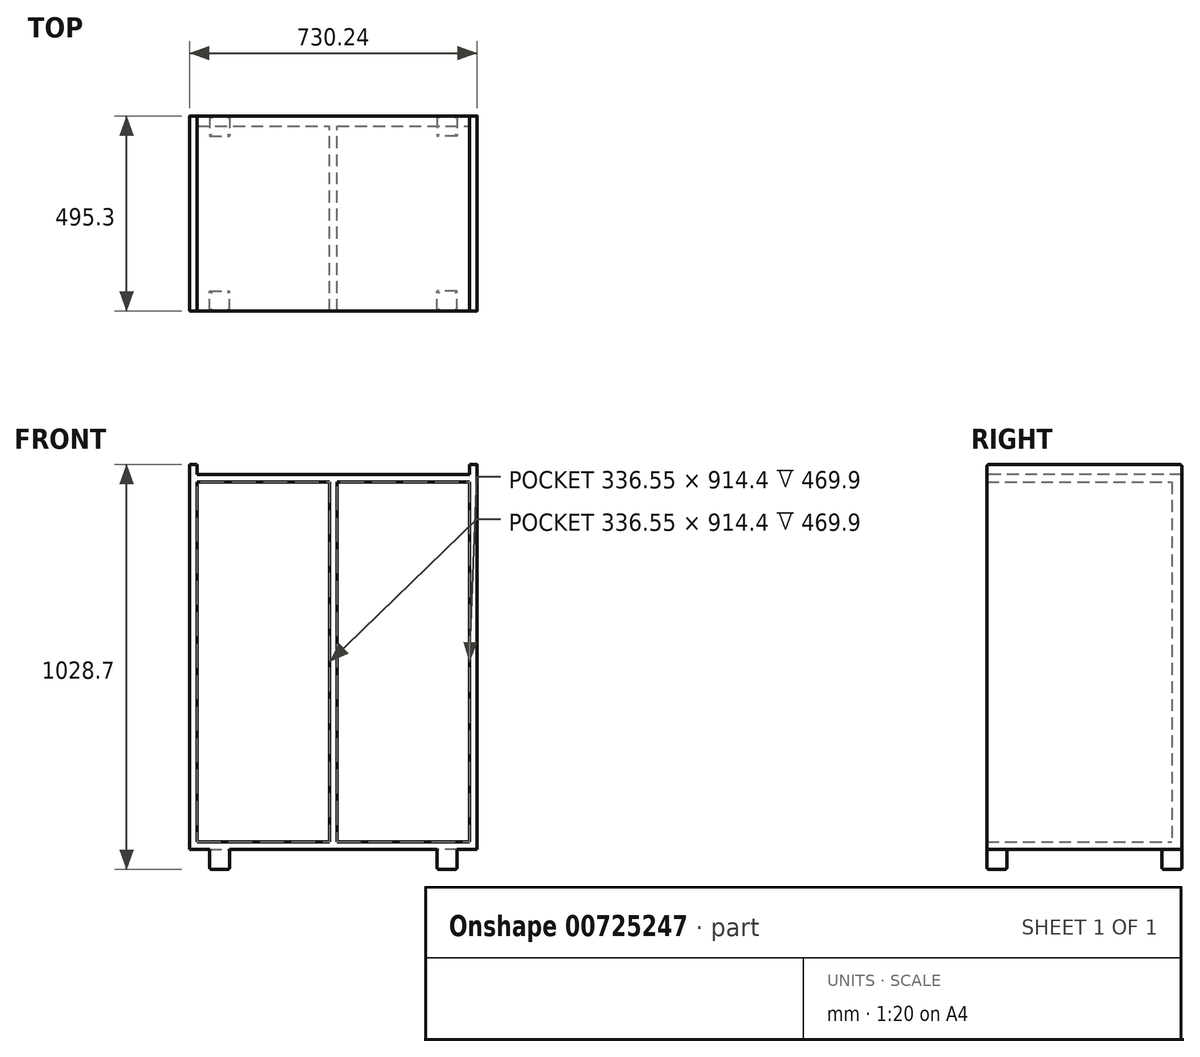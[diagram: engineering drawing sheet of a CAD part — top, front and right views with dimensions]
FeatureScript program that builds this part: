
annotation { "Feature Type Name" : "Feature", "Feature Type Description" : "" }
export const myFeature = defineFeature(function(context is Context, id is Id, definition is map)
    precondition{}
    {
        {
            var Q0;
            Q0=qCreatedBy(makeId("Top.planeOp"),FACE);
            var sketch = newSketch(context, id + "F0", { "sketchPlane" : qUnion([Q0])});
            skLineSegment(sketch, "E0.bottom", {"start": v(365.13, 247.65) * mm, "end": v(-365.12, 247.65) * mm});
            skLineSegment(sketch, "E0.top", {"start": v(365.12, -247.65) * mm, "end": v(-365.13, -247.65) * mm});
            skLineSegment(sketch, "E0.left", {"start": v(365.13, 247.65) * mm, "end": v(365.12, -247.65) * mm});
            skLineSegment(sketch, "E0.right", {"start": v(-365.12, 247.65) * mm, "end": v(-365.13, -247.65) * mm});
            skPoint(sketch, "E0.middle", {"position": v(0, 0) * mm});
            skSolve(sketch);
        }
        {
            var Q0;
            Q0 = qSketchRegion(id + "F0", true);
            extrude(context, id + "F1", {"entities" : qUnion([Q0]), "depth" : 977.9 * mm, "offsetDistance" : 25.4 * mm});
        }
        {
            var Q0;
            Q0=makeQuery(id+"F1.opExtrude","CAP_FACE",FACE,{"disambiguationData":[OSD([sQuery(id+"F0.wireOp",EDGE,"E0.bottom"),sQuery(id+"F0.wireOp",EDGE,"E0.top"),sQuery(id+"F0.wireOp",EDGE,"E0.left"),sQuery(id+"F0.wireOp",EDGE,"E0.right")])],"isStart":false});
            var sketch = newSketch(context, id + "F2", { "sketchPlane" : qUnion([Q0])});
            skLineSegment(sketch, "E1.bottom", {"start": v(346.08, 247.65) * mm, "end": v(-346.08, 247.65) * mm});
            skLineSegment(sketch, "E1.top", {"start": v(346.08, -247.65) * mm, "end": v(-346.08, -247.65) * mm});
            skLineSegment(sketch, "E1.left", {"start": v(346.08, 247.65) * mm, "end": v(346.08, -247.65) * mm});
            skLineSegment(sketch, "E1.right", {"start": v(-346.08, 247.65) * mm, "end": v(-346.08, -247.65) * mm});
            skPoint(sketch, "E1.middle", {"position": v(0, 0) * mm});
            skSolve(sketch);
        }
        {
            var Q0;
            Q0 = qSketchRegion(id + "F2", true);
            extrude(context, id + "F3", {"entities" : qUnion([Q0]), "operationType" : NewBodyOperationType.REMOVE, "oppositeDirection" : true, "depth" : 25.4 * mm, "offsetDistance" : 25.4 * mm});
        }
        {
            var Q0;
            Q0=makeQuery(id+"F1.opExtrude","SWEPT_FACE",FACE,{"disambiguationData":[OSD([sQuery(id+"F0.wireOp",EDGE,"E0.top")])]});
            var sketch = newSketch(context, id + "F4", { "sketchPlane" : qUnion([Q0])});
            skLineSegment(sketch, "E2.bottom", {"start": v(-346.08, 933.45) * mm, "end": v(346.07, 933.45) * mm});
            skLineSegment(sketch, "E2.top", {"start": v(-346.08, 19.05) * mm, "end": v(346.07, 19.05) * mm});
            skLineSegment(sketch, "E2.left", {"start": v(-346.08, 933.45) * mm, "end": v(-346.08, 19.05) * mm});
            skLineSegment(sketch, "E2.right", {"start": v(346.07, 933.45) * mm, "end": v(346.07, 19.05) * mm});
            skSolve(sketch);
        }
        {
            var Q0;
            Q0 = qSketchRegion(id + "F4", true);
            extrude(context, id + "F5", {"entities" : qUnion([Q0]), "operationType" : NewBodyOperationType.REMOVE, "oppositeDirection" : true, "depth" : 469.9 * mm, "offsetDistance" : 25.4 * mm});
        }
        {
            var Q0;
            Q0=makeQuery(id+"F5.boolean.opBoolean","COPY",FACE,{"derivedFrom":makeQuery(id+"F5.opExtrude","CAP_FACE",FACE,{"disambiguationData":[OSD([sQuery(id+"F4.wireOp",EDGE,"E2.bottom"),sQuery(id+"F4.wireOp",EDGE,"E2.top"),sQuery(id+"F4.wireOp",EDGE,"E2.left"),sQuery(id+"F4.wireOp",EDGE,"E2.right")])],"isStart":false})});
            var sketch = newSketch(context, id + "F6", { "sketchPlane" : qUnion([Q0])});
            skLineSegment(sketch, "E3", {"start": v(-346.08, 933.45) * mm, "end": v(346.07, 19.05) * mm, "construction": true});
            skLineSegment(sketch, "E4", {"start": v(346.07, 933.45) * mm, "end": v(-346.08, 19.05) * mm, "construction": true});
            skPoint(sketch, "E5", {"position": v(0, 476.25) * mm});
            skLineSegment(sketch, "E6.bottom", {"start": v(-9.53, 933.45) * mm, "end": v(9.52, 933.45) * mm});
            skLineSegment(sketch, "E6.top", {"start": v(-9.52, 19.05) * mm, "end": v(9.53, 19.05) * mm});
            skLineSegment(sketch, "E6.left", {"start": v(-9.53, 933.45) * mm, "end": v(-9.52, 19.05) * mm});
            skLineSegment(sketch, "E6.right", {"start": v(9.52, 933.45) * mm, "end": v(9.53, 19.05) * mm});
            skSolve(sketch);
        }
        {
            var Q0;
            Q0 = qSketchRegion(id + "F6", true);
            extrude(context, id + "F7", {"entities" : qUnion([Q0]), "operationType" : NewBodyOperationType.ADD, "depth" : 469.9 * mm, "offsetDistance" : 25.4 * mm});
        }
        {
            var Q0;
            Q0=makeQuery(id+"F1.opExtrude","CAP_FACE",FACE,{"disambiguationData":[OSD([sQuery(id+"F0.wireOp",EDGE,"E0.bottom"),sQuery(id+"F0.wireOp",EDGE,"E0.top"),sQuery(id+"F0.wireOp",EDGE,"E0.left"),sQuery(id+"F0.wireOp",EDGE,"E0.right")])],"isStart":true});
            var sketch = newSketch(context, id + "F8", { "sketchPlane" : qUnion([Q0])});
            skLineSegment(sketch, "E7.bottom", {"start": v(314.33, 247.65) * mm, "end": v(-314.33, 247.65) * mm, "construction": true});
            skLineSegment(sketch, "E7.top", {"start": v(314.33, -247.65) * mm, "end": v(-314.33, -247.65) * mm, "construction": true});
            skLineSegment(sketch, "E7.left", {"start": v(314.32, 247.65) * mm, "end": v(314.33, -247.65) * mm, "construction": true});
            skLineSegment(sketch, "E7.right", {"start": v(-314.33, 247.65) * mm, "end": v(-314.32, -247.65) * mm, "construction": true});
            skPoint(sketch, "E7.middle", {"position": v(0, 0) * mm});
            skLineSegment(sketch, "E8.bottom", {"start": v(314.33, 247.65) * mm, "end": v(263.53, 247.65) * mm});
            skLineSegment(sketch, "E8.top", {"start": v(314.33, 196.85) * mm, "end": v(263.53, 196.85) * mm});
            skLineSegment(sketch, "E8.left", {"start": v(314.33, 247.65) * mm, "end": v(314.33, 196.85) * mm});
            skLineSegment(sketch, "E8.right", {"start": v(263.53, 247.65) * mm, "end": v(263.53, 196.85) * mm});
            skLineSegment(sketch, "E9.bottom", {"start": v(314.33, -247.65) * mm, "end": v(263.53, -247.65) * mm});
            skLineSegment(sketch, "E9.top", {"start": v(314.33, -196.85) * mm, "end": v(263.53, -196.85) * mm});
            skLineSegment(sketch, "E9.left", {"start": v(314.33, -247.65) * mm, "end": v(314.33, -196.85) * mm});
            skLineSegment(sketch, "E9.right", {"start": v(263.53, -247.65) * mm, "end": v(263.53, -196.85) * mm});
            skLineSegment(sketch, "E10.bottom", {"start": v(-314.33, -247.65) * mm, "end": v(-263.52, -247.65) * mm});
            skLineSegment(sketch, "E10.top", {"start": v(-314.33, -196.85) * mm, "end": v(-263.52, -196.85) * mm});
            skLineSegment(sketch, "E10.left", {"start": v(-314.33, -247.65) * mm, "end": v(-314.33, -196.85) * mm});
            skLineSegment(sketch, "E10.right", {"start": v(-263.52, -247.65) * mm, "end": v(-263.52, -196.85) * mm});
            skLineSegment(sketch, "E11.bottom", {"start": v(-314.33, 247.65) * mm, "end": v(-263.53, 247.65) * mm});
            skLineSegment(sketch, "E11.top", {"start": v(-314.33, 196.85) * mm, "end": v(-263.53, 196.85) * mm});
            skLineSegment(sketch, "E11.left", {"start": v(-314.33, 247.65) * mm, "end": v(-314.33, 196.85) * mm});
            skLineSegment(sketch, "E11.right", {"start": v(-263.53, 247.65) * mm, "end": v(-263.53, 196.85) * mm});
            skSolve(sketch);
        }
        {
            var Q0;
            Q0 = qSketchRegion(id + "F8", true);
            extrude(context, id + "F9", {"entities" : qUnion([Q0]), "operationType" : NewBodyOperationType.ADD, "depth" : 50.8 * mm, "offsetDistance" : 25.4 * mm});
        }
        {
            var Q0;
            Q0=makeQuery(id+"F9.opExtrude","CAP_EDGE",EDGE,{"disambiguationData":[OSD([sQuery(id+"F8.wireOp",EDGE,"E11.right")])],"isStart":false});
            var Q1;
            Q1=makeQuery(id+"F9.opExtrude","CAP_EDGE",EDGE,{"disambiguationData":[OSD([sQuery(id+"F8.wireOp",EDGE,"E11.top")])],"isStart":false});
            var Q2;
            Q2=makeQuery(id+"F9.opExtrude","CAP_EDGE",EDGE,{"disambiguationData":[OSD([sQuery(id+"F8.wireOp",EDGE,"E11.bottom")])],"isStart":false});
            var Q3;
            Q3=makeQuery(id+"F9.opExtrude","CAP_EDGE",EDGE,{"disambiguationData":[OSD([sQuery(id+"F8.wireOp",EDGE,"E11.left")])],"isStart":false});
            var Q4;
            Q4=makeQuery(id+"F9.opExtrude","CAP_EDGE",EDGE,{"disambiguationData":[OSD([sQuery(id+"F8.wireOp",EDGE,"E10.left")])],"isStart":false});
            var Q5;
            Q5=makeQuery(id+"F9.opExtrude","CAP_EDGE",EDGE,{"disambiguationData":[OSD([sQuery(id+"F8.wireOp",EDGE,"E10.top")])],"isStart":false});
            var Q6;
            Q6=makeQuery(id+"F9.opExtrude","CAP_EDGE",EDGE,{"disambiguationData":[OSD([sQuery(id+"F8.wireOp",EDGE,"E10.right")])],"isStart":false});
            var Q7;
            Q7=makeQuery(id+"F9.opExtrude","CAP_EDGE",EDGE,{"disambiguationData":[OSD([sQuery(id+"F8.wireOp",EDGE,"E10.bottom")])],"isStart":false});
            fillet(context, id + "F10", {"entities" : qUnion([Q0, Q1, Q2, Q3, Q4, Q5, Q6, Q7]), "radius" : 5.08 * mm, "tangentPropagation" : true, "allowEdgeOverflow" : false});
        }
        {
            var Q0;
            Q0=makeQuery(id+"F9.opExtrude","CAP_EDGE",EDGE,{"disambiguationData":[OSD([sQuery(id+"F8.wireOp",EDGE,"E8.left")])],"isStart":false});
            var Q1;
            Q1=makeQuery(id+"F9.opExtrude","CAP_EDGE",EDGE,{"disambiguationData":[OSD([sQuery(id+"F8.wireOp",EDGE,"E8.bottom")])],"isStart":false});
            var Q2;
            Q2=makeQuery(id+"F9.opExtrude","CAP_EDGE",EDGE,{"disambiguationData":[OSD([sQuery(id+"F8.wireOp",EDGE,"E8.right")])],"isStart":false});
            var Q3;
            Q3=makeQuery(id+"F9.opExtrude","CAP_EDGE",EDGE,{"disambiguationData":[OSD([sQuery(id+"F8.wireOp",EDGE,"E8.top")])],"isStart":false});
            fillet(context, id + "F11", {"entities" : qUnion([Q0, Q1, Q2, Q3]), "radius" : 5.08 * mm, "tangentPropagation" : true, "allowEdgeOverflow" : false});
        }
        {
            var Q0;
            Q0=makeQuery(id+"F9.opExtrude","CAP_EDGE",EDGE,{"disambiguationData":[OSD([sQuery(id+"F8.wireOp",EDGE,"E9.bottom")])],"isStart":false});
            var Q1;
            Q1=makeQuery(id+"F9.opExtrude","CAP_EDGE",EDGE,{"disambiguationData":[OSD([sQuery(id+"F8.wireOp",EDGE,"E9.left")])],"isStart":false});
            var Q2;
            Q2=makeQuery(id+"F9.opExtrude","CAP_EDGE",EDGE,{"disambiguationData":[OSD([sQuery(id+"F8.wireOp",EDGE,"E9.top")])],"isStart":false});
            var Q3;
            Q3=makeQuery(id+"F9.opExtrude","CAP_EDGE",EDGE,{"disambiguationData":[OSD([sQuery(id+"F8.wireOp",EDGE,"E9.right")])],"isStart":false});
            fillet(context, id + "F12", {"entities" : qUnion([Q0, Q1, Q2, Q3]), "radius" : 5.08 * mm, "tangentPropagation" : true, "allowEdgeOverflow" : false});
        }
        {
            var Q0;
            {var subQ0=sQuery(id+"F0.wireOp",EDGE,"E0.left");var subQ1=sQuery(id+"F0.wireOp",EDGE,"E0.top");Q0=makeQuery(id+"F3.boolean.opBoolean","SPLIT",EDGE,{"disambiguationData":[TD([makeQuery(id+"F1.opExtrude","SWEPT_FACE",FACE,{"disambiguationData":[OSD([subQ0])]})])],"derivedFrom":makeQuery(id+"F1.opExtrude","CAP_EDGE",EDGE,{"disambiguationData":[OSD([subQ1])],"isStart":false})});}
            var Q1;
            {var subQ0=sQuery(id+"F0.wireOp",EDGE,"E0.bottom");var subQ1=sQuery(id+"F0.wireOp",EDGE,"E0.left");Q1=makeQuery(id+"F3.boolean.opBoolean","SPLIT",EDGE,{"disambiguationData":[TD([makeQuery(id+"F1.opExtrude","SWEPT_FACE",FACE,{"disambiguationData":[OSD([subQ1])]})])],"derivedFrom":makeQuery(id+"F1.opExtrude","CAP_EDGE",EDGE,{"disambiguationData":[OSD([subQ0])],"isStart":false})});}
            var Q2;
            {var subQ0=sQuery(id+"F0.wireOp",EDGE,"E0.right");var subQ1=sQuery(id+"F0.wireOp",EDGE,"E0.top");Q2=makeQuery(id+"F3.boolean.opBoolean","SPLIT",EDGE,{"disambiguationData":[TD([makeQuery(id+"F1.opExtrude","SWEPT_FACE",FACE,{"disambiguationData":[OSD([subQ0])]})])],"derivedFrom":makeQuery(id+"F1.opExtrude","CAP_EDGE",EDGE,{"disambiguationData":[OSD([subQ1])],"isStart":false})});}
            var Q3;
            {var subQ0=sQuery(id+"F0.wireOp",EDGE,"E0.bottom");var subQ1=sQuery(id+"F0.wireOp",EDGE,"E0.right");Q3=makeQuery(id+"F3.boolean.opBoolean","SPLIT",EDGE,{"disambiguationData":[TD([makeQuery(id+"F1.opExtrude","SWEPT_FACE",FACE,{"disambiguationData":[OSD([subQ1])]})])],"derivedFrom":makeQuery(id+"F1.opExtrude","CAP_EDGE",EDGE,{"disambiguationData":[OSD([subQ0])],"isStart":false})});}
            fillet(context, id + "F13", {"entities" : qUnion([Q0, Q1, Q2, Q3]), "radius" : 5.08 * mm, "tangentPropagation" : true, "allowEdgeOverflow" : false});
        }
    });
